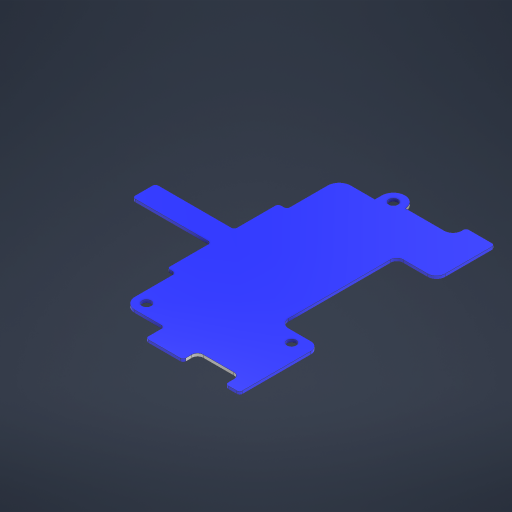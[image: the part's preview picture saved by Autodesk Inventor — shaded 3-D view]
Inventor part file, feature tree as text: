
AUTODESK INVENTOR PART (.ipt)
format: ipt  version: 2024 (Build 280153000, 153)  size: 346,112 bytes
history: native  units: in
note: dims shown in document units (in); Inventor stores cm internally (conversion verified against a paired STEP export)
features: plane x1, extrude x1, sketch x1
ambient origin geometry x8: Origin, YZ Plane, XZ Plane, XY Plane, X Axis, Y Axis, Z Axis, Center Point
bodies: Body1 (feature_tree)
feature tree (3):
  plane  "Work Plane2"
  extrude  "Extrusion2"  Depth=0.0394in TaperAngle=0.0deg
  sketch  "Sketch2"  dims[d13=0.122in d15=0.122in d16=0.0394in d17=0.0in d26=0.0394in d27=0.1181in d30=0.1181in d32=0.0394in d33=0.7957in d36=0.5512in d37=0.1181in d38=0.5512in d39=0.1181in d40=0.0394in d41=1.4173in d42=0.5118in d43=0.0394in d45=0.1495in d46=1.5841in d47=3.4646in d49=0.1575in d50=0.0787in d51=0.0787in d52=0.0197in]
